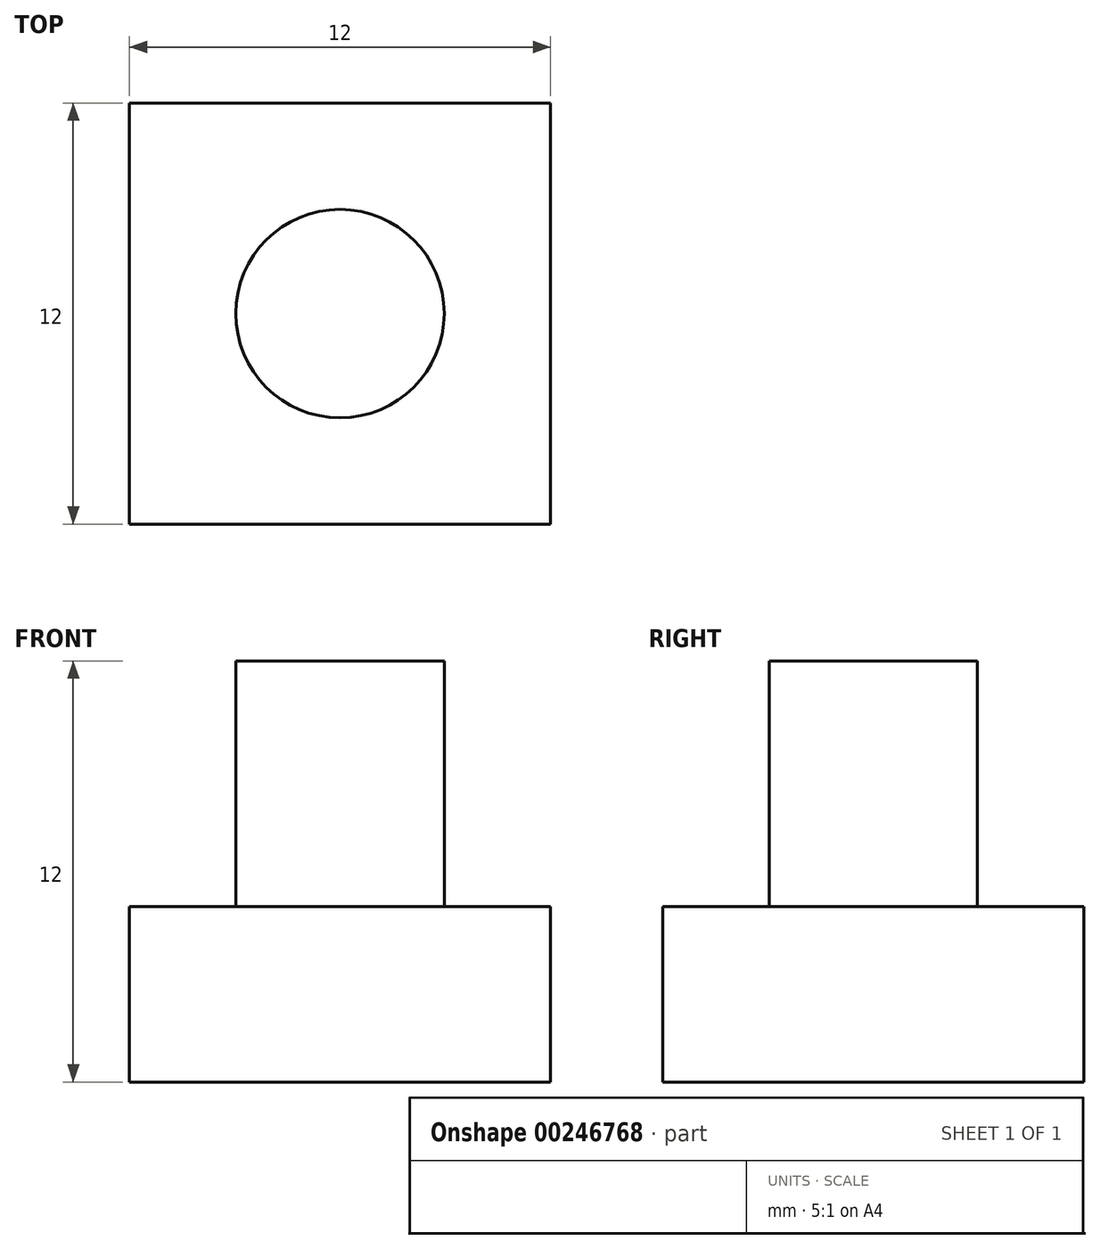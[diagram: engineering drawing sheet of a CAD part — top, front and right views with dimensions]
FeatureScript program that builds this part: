
annotation { "Feature Type Name" : "Feature", "Feature Type Description" : "" }
export const myFeature = defineFeature(function(context is Context, id is Id, definition is map)
    precondition{}
    {
        {
            var Q0;
            Q0=qCreatedBy(makeId("Top.planeOp"),FACE);
            var sketch = newSketch(context, id + "F0", { "sketchPlane" : qUnion([Q0])});
            skLineSegment(sketch, "E0.bottom", {"start": v(0, 0) * mm, "end": v(12, 0) * mm});
            skLineSegment(sketch, "E0.top", {"start": v(0, 12) * mm, "end": v(12, 12) * mm});
            skLineSegment(sketch, "E0.left", {"start": v(0, 0) * mm, "end": v(0, 12) * mm});
            skLineSegment(sketch, "E0.right", {"start": v(12, 0) * mm, "end": v(12, 12) * mm});
            skSolve(sketch);
        }
        {
            var Q0;
            Q0=makeQuery(id+"F0.imprint","IMPRINT",FACE,{"disambiguationData":[TD([[makeQuery(id+"F0.imprint","IMPRINT",EDGE,{"derivedFrom":sQuery(id+"F0.wireOp",EDGE,"E0.bottom")}),1.0]])]});
            extrude(context, id + "F1", {"entities" : qUnion([Q0]), "depth" : 5 * mm});
        }
        {
            var Q0;
            Q0=makeQuery(id+"F1.opExtrude","CAP_FACE",FACE,{"disambiguationData":[OSD([sQuery(id+"F0.wireOp",EDGE,"E0.bottom"),sQuery(id+"F0.wireOp",EDGE,"E0.top"),sQuery(id+"F0.wireOp",EDGE,"E0.left"),sQuery(id+"F0.wireOp",EDGE,"E0.right")])],"isStart":false});
            var sketch = newSketch(context, id + "F2", { "sketchPlane" : qUnion([Q0])});
            skCircle(sketch, "E1", {"center": v(6, 6) * mm, "radius": 2.97 * mm});
            skPoint(sketch, "E1.centerSnap0", {"position": v(6, 12) * mm});
            skPoint(sketch, "E1.centerSnap1", {"position": v(0, 6) * mm});
            skSolve(sketch);
        }
        {
            var Q0;
            Q0=makeQuery(id+"F2.imprint","IMPRINT",FACE,{"disambiguationData":[TD([[makeQuery(id+"F2.imprint","IMPRINT",EDGE,{"derivedFrom":sQuery(id+"F2.wireOp",EDGE,"E1")}),1.0]])]});
            extrude(context, id + "F3", {"entities" : qUnion([Q0]), "operationType" : NewBodyOperationType.ADD, "depth" : 7 * mm});
        }
    });
